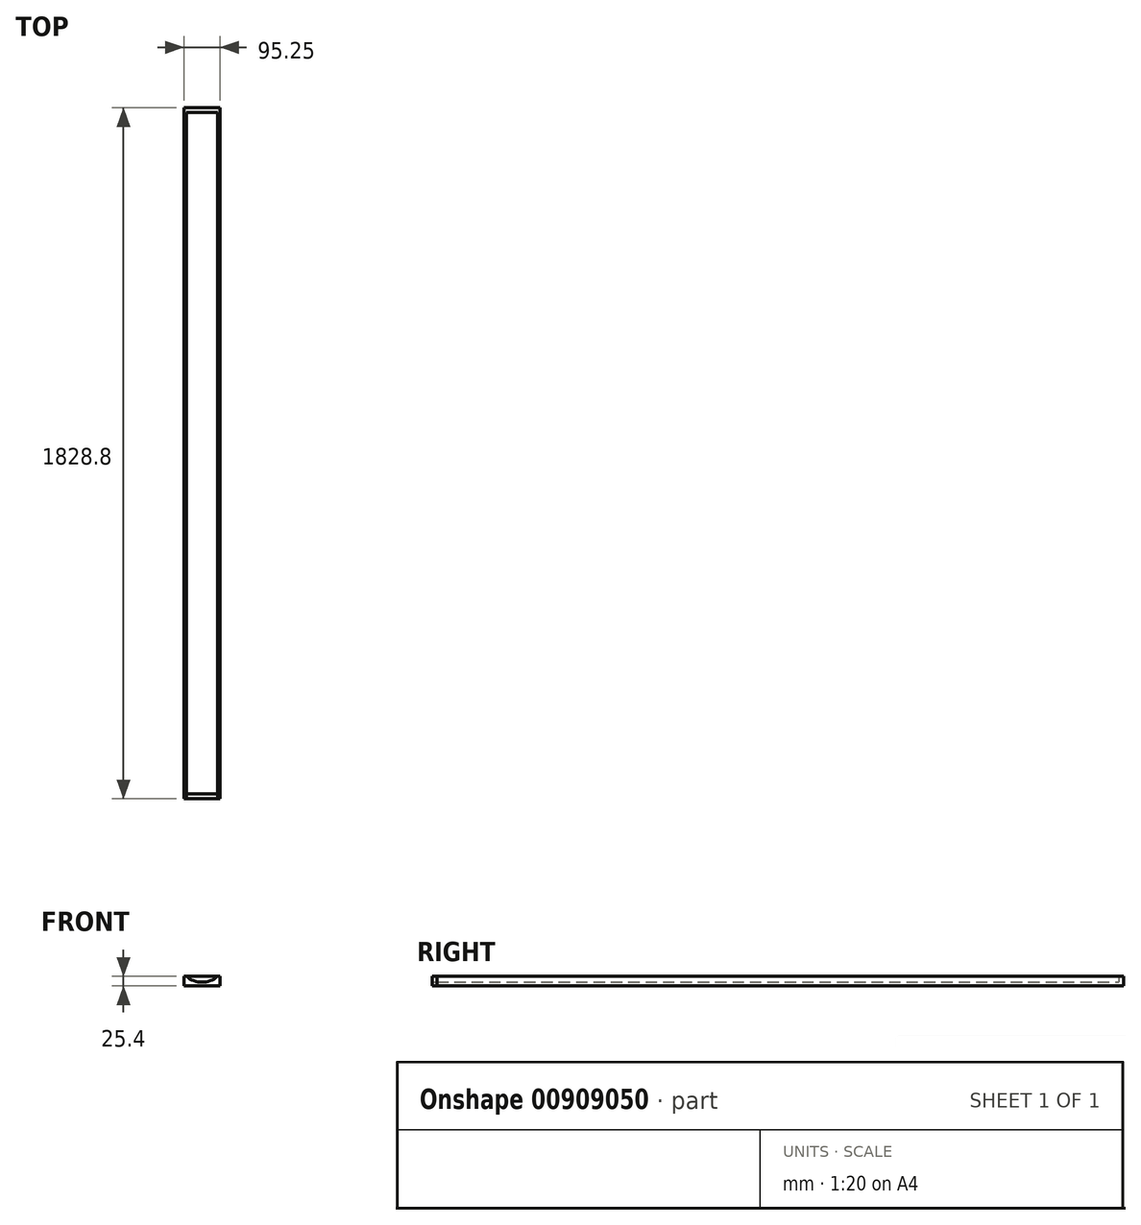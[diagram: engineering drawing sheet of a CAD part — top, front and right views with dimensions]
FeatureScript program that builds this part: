
annotation { "Feature Type Name" : "Feature", "Feature Type Description" : "" }
export const myFeature = defineFeature(function(context is Context, id is Id, definition is map)
    precondition{}
    {
        {
            var Q0;
            Q0=qCreatedBy(makeId("Front.planeOp"),FACE);
            var sketch = newSketch(context, id + "F0", { "sketchPlane" : qUnion([Q0])});
            skLineSegment(sketch, "E0.bottom", {"start": v(0, 0) * mm, "end": v(95.25, 0) * mm});
            skLineSegment(sketch, "E0.top", {"start": v(0, 25.4) * mm, "end": v(6.35, 25.4) * mm});
            skLineSegment(sketch, "E0.left", {"start": v(0, 0) * mm, "end": v(0, 25.4) * mm});
            skLineSegment(sketch, "E0.right", {"start": v(95.25, 0) * mm, "end": v(95.25, 25.4) * mm});
            skLineSegment(sketch, "E1.bottom", {"start": v(0, 0) * mm, "end": v(6.35, 0) * mm});
            skLineSegment(sketch, "E2.bottom", {"start": v(95.25, 25.4) * mm, "end": v(88.9, 25.4) * mm});
            skLineSegment(sketch, "E2.top", {"start": v(95.25, 0) * mm, "end": v(88.9, 0) * mm});
            skLineSegment(sketch, "E2.left", {"start": v(95.25, 25.4) * mm, "end": v(95.25, 0) * mm});
            skArc(sketch, "E3", {"start": v(6.35, 25.4) * mm, "mid": v(47.63, 10.16) * mm, "end": v(88.9, 25.4) * mm});
            skLineSegment(sketch, "E4.trimOffspring", {"start": v(88.9, 25.4) * mm, "end": v(95.25, 25.4) * mm});
            skSolve(sketch);
        }
        {
            var Q0;
            Q0=makeQuery(id+"F0.imprint","IMPRINT",FACE,{"disambiguationData":[TD([[makeQuery(id+"F0.imprint","IMPRINT",EDGE,{"derivedFrom":sQuery(id+"F0.wireOp",EDGE,"E0.bottom")}),1.0]])]});
            extrude(context, id + "F1", {"entities" : qUnion([Q0]), "depth" : 1803.4 * mm, "offsetDistance" : 25.4 * mm});
        }
        {
            var Q0;
            Q0=qCreatedBy(makeId("Top.planeOp"),FACE);
            var sketch = newSketch(context, id + "F2", { "sketchPlane" : qUnion([Q0])});
            skLineSegment(sketch, "E5.bottom", {"start": v(95.25, 0) * mm, "end": v(0, 0) * mm});
            skLineSegment(sketch, "E5.top", {"start": v(95.25, 12.7) * mm, "end": v(0, 12.7) * mm});
            skLineSegment(sketch, "E5.left", {"start": v(95.25, 0) * mm, "end": v(95.25, 12.7) * mm});
            skLineSegment(sketch, "E5.right", {"start": v(0, 0) * mm, "end": v(0, 12.7) * mm});
            skSolve(sketch);
        }
        {
            var Q0;
            Q0=makeQuery(id+"F2.imprint","IMPRINT",FACE,{"disambiguationData":[TD([[makeQuery(id+"F2.imprint","IMPRINT",EDGE,{"derivedFrom":sQuery(id+"F2.wireOp",EDGE,"E5.bottom")}),-1.0]])]});
            extrude(context, id + "F3", {"entities" : qUnion([Q0]), "operationType" : NewBodyOperationType.ADD, "depth" : 25.4 * mm, "offsetDistance" : 25.4 * mm});
        }
        {
            var Q0;
            Q0=makeQuery(id+"F1.opExtrude","CAP_FACE",FACE,{"disambiguationData":[OSD([sQuery(id+"F0.wireOp",EDGE,"E0.bottom"),sQuery(id+"F0.wireOp",EDGE,"E1.bottom"),sQuery(id+"F0.wireOp",EDGE,"E0.top"),sQuery(id+"F0.wireOp",EDGE,"E0.left"),sQuery(id+"F0.wireOp",EDGE,"E2.top"),sQuery(id+"F0.wireOp",EDGE,"E2.left"),sQuery(id+"F0.wireOp",EDGE,"E3"),sQuery(id+"F0.wireOp",EDGE,"E4.trimOffspring")])],"isStart":false});
            var sketch = newSketch(context, id + "F4", { "sketchPlane" : qUnion([Q0])});
            skLineSegment(sketch, "E6.bottom", {"start": v(0, 25.4) * mm, "end": v(95.25, 25.4) * mm});
            skLineSegment(sketch, "E6.top", {"start": v(0, 0) * mm, "end": v(95.25, 0) * mm});
            skLineSegment(sketch, "E6.left", {"start": v(0, 25.4) * mm, "end": v(0, 0) * mm});
            skLineSegment(sketch, "E6.right", {"start": v(95.25, 25.4) * mm, "end": v(95.25, 0) * mm});
            skSolve(sketch);
        }
        {
            var Q0;
            {var subQ1=makeQuery(id+"F1.opExtrude","CAP_EDGE",EDGE,{"disambiguationData":[OSD([sQuery(id+"F0.wireOp",EDGE,"E3")])],"isStart":false});Q0=makeQuery(id+"F4.imprint","IMPRINT",FACE,{"disambiguationData":[TD([[makeQuery(id+"F4.imprint","IMPRINT",EDGE,{"derivedFrom":subQ1}),1.0]])]});}
            extrude(context, id + "F5", {"entities" : qUnion([Q0]), "depth" : 12.7 * mm, "offsetDistance" : 25.4 * mm});
        }
        {
            var Q0;
            Q0=makeQuery(id+"F1.opExtrude","CAP_FACE",FACE,{"disambiguationData":[OSD([sQuery(id+"F0.wireOp",EDGE,"E0.bottom"),sQuery(id+"F0.wireOp",EDGE,"E1.bottom"),sQuery(id+"F0.wireOp",EDGE,"E0.top"),sQuery(id+"F0.wireOp",EDGE,"E0.left"),sQuery(id+"F0.wireOp",EDGE,"E2.top"),sQuery(id+"F0.wireOp",EDGE,"E2.left"),sQuery(id+"F0.wireOp",EDGE,"E3"),sQuery(id+"F0.wireOp",EDGE,"E4.trimOffspring")])],"isStart":false});
            extrude(context, id + "F6", {"entities" : qUnion([Q0]), "depth" : 12.7 * mm, "offsetDistance" : 25.4 * mm});
        }
    });
